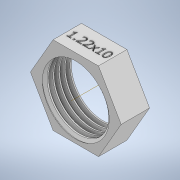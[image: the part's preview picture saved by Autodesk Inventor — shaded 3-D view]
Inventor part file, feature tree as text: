
AUTODESK INVENTOR PART (.ipt)
format: ipt  version: 2021.1 (Build 251245010, 245A)  size: 545,792 bytes
history: native  units: in
note: dims shown in document units (in); Inventor stores cm internally (conversion verified against a paired STEP export)
features: sketch x5, extrude x4, helix x1
ambient origin geometry x8: Origin, YZ Plane, XZ Plane, XY Plane, X Axis, Y Axis, Z Axis, Center Point
bodies: Solid1 (feature_tree)
feature tree (10):
  extrude  "Extrusion1"  Depth=0.125in
  helix  "Coil1"  [1 undecoded]
  extrude  "Extrusion2"  TaperAngle=60.0deg  [1 undecoded]
  extrude  "Extrusion3"  Depth=0.0072in
  extrude  "Extrusion4"  TaperAngle=120.0deg  [1 undecoded]
  sketch  "Sketch1"  dims[d0=1.1327in d1=0.125in d2=0.5in d3=0.0in]
  sketch  "Sketch2"  dims[d4=0.0072in d5=60.0deg]
  sketch  "Sketch3"  dims[d7=120.0deg d8=0.0072in]
  sketch  "Sketch4"  dims[d9=60.0deg d10=120.0deg]
  sketch  "Sketch5"  dims[d11=0.1in d12=0.05in d13=0.5664in d15=0.1in d16=0.7in d17=0.3937in d18=0.0in d19=90.0deg d20=90.0deg d21=0.0in d22=0.0in d23=0.5in d24=0.0in d25=0.6236in d26=0.05in d27=0.0in d28=0.05in d29=0.0in]
note: 3 required parameter values undecoded (feature->parameter linkage not recoverable at this tier; creation-order binding heuristic only, values carry confidence <= 0.55)
